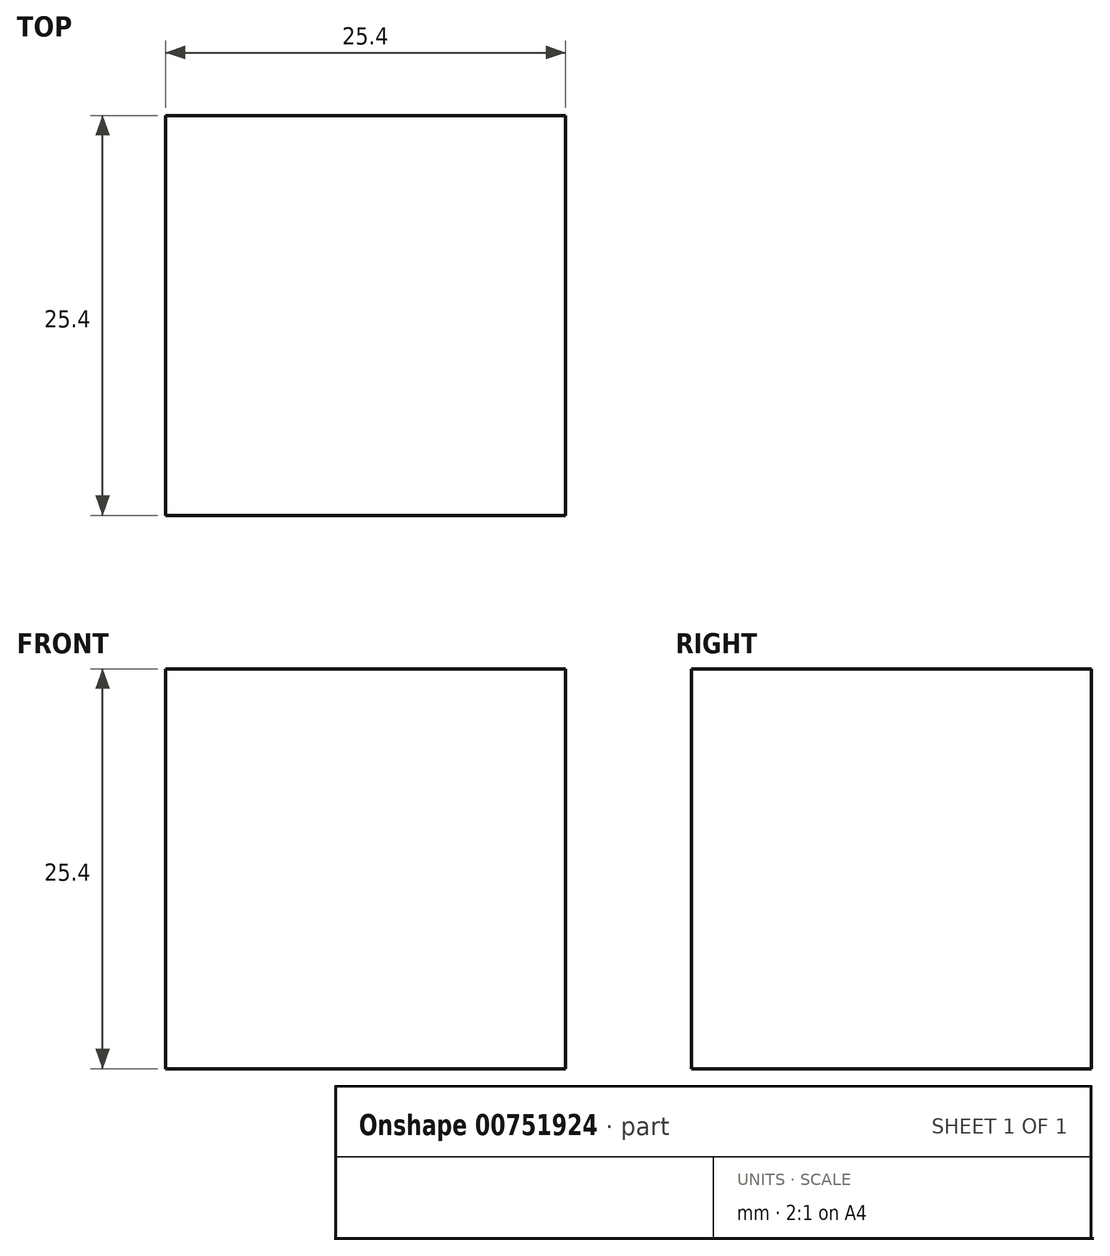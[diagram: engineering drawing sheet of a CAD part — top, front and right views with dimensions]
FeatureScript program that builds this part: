
annotation { "Feature Type Name" : "Feature", "Feature Type Description" : "" }
export const myFeature = defineFeature(function(context is Context, id is Id, definition is map)
    precondition{}
    {
        {
            var Q0;
            Q0=qCreatedBy(makeId("Front.planeOp"),FACE);
            var sketch = newSketch(context, id + "F0", { "sketchPlane" : qUnion([Q0])});
            skLineSegment(sketch, "E0", {"start": v(-12.7, 0) * mm, "end": v(-12.7, 25.4) * mm});
            skLineSegment(sketch, "E1", {"start": v(-12.7, 25.4) * mm, "end": v(12.7, 25.4) * mm});
            skLineSegment(sketch, "E2", {"start": v(12.7, 25.4) * mm, "end": v(12.7, 0) * mm});
            skLineSegment(sketch, "E3", {"start": v(12.7, 0) * mm, "end": v(-12.7, 0) * mm});
            skSolve(sketch);
        }
        {
            var Q0;
            Q0=makeQuery(id+"F0.imprint","IMPRINT",FACE,{"disambiguationData":[TD([[makeQuery(id+"F0.imprint","IMPRINT",EDGE,{"derivedFrom":sQuery(id+"F0.wireOp",EDGE,"E0")}),-1.0]])]});
            extrude(context, id + "F1", {"entities" : qUnion([Q0]), "oppositeDirection" : true, "depth" : 25.4 * mm, "offsetDistance" : 25.4 * mm});
        }
    });
